# Revit family: РДС-32
name_source: partatom
category: Арматура трубопроводов
units: mm (PartAtom-declared; Revit-internal decimal feet)

## family parameters
Всегда вертикально = Да
На основе рабочей плоскости = Нет
Общий = Нет
При загрузке вырезать с полостями = Нет
Размер круглого соединителя = Использовать диаметр
Тип детали = Клапан - Вставляется

## types (6) — shared parameters
ADSK_Единица измерения = шт.
ADSK_Завод-изготовитель = РУП "БЕЛГАЗТЕХНИКА"
ADSK_Количество = 1
ADSK_Марка = РДС-32
ADSK_Масса_Текст = 12,5 кг
ADSK_Тип соединения = фланцевый
zero-valued in all types: Отметка по умолчанию

## per-type parameters (varying)
| type | 1.5.6 | 2.3.4 | 5.6 | ADSK_Диапазон выходного давления, МПа | ADSK_Наименование | ADSK_Наличие сбросного клапана (ПСК) |
| РДС-32-1 | Да | Нет | Нет | 0,005-0,015 | Регулятор РДС-32-1 ТУ РБ 100270876.099-2002 | нет |
| РДС-32-2 | Нет | Да | Нет | 0,015-0,05 | Регулятор РДС-32-2 ТУ РБ 100270876.099-2002 | нет |
| РДС-32-3 | Нет | Да | Нет | 0,05-0,1 | Регулятор РДС-32-3 ТУ РБ 100270876.099-2002 | нет |
| РДС-32-4 | Нет | Да | Нет | 0,1-0,3 | Регулятор РДС-32-4 ТУ РБ 100270876.099-2002 | нет |
| РДС-32-5 | Да | Нет | Да | 0,0013-0,0028 | Регулятор РДС-32-5 ТУ РБ 100270876.099-2002 | да |
| РДС-32-6 | Да | Нет | Да | 0,0026-0,0054 | Регулятор РДС-32-6 ТУ РБ 100270876.099-2002 | да |
